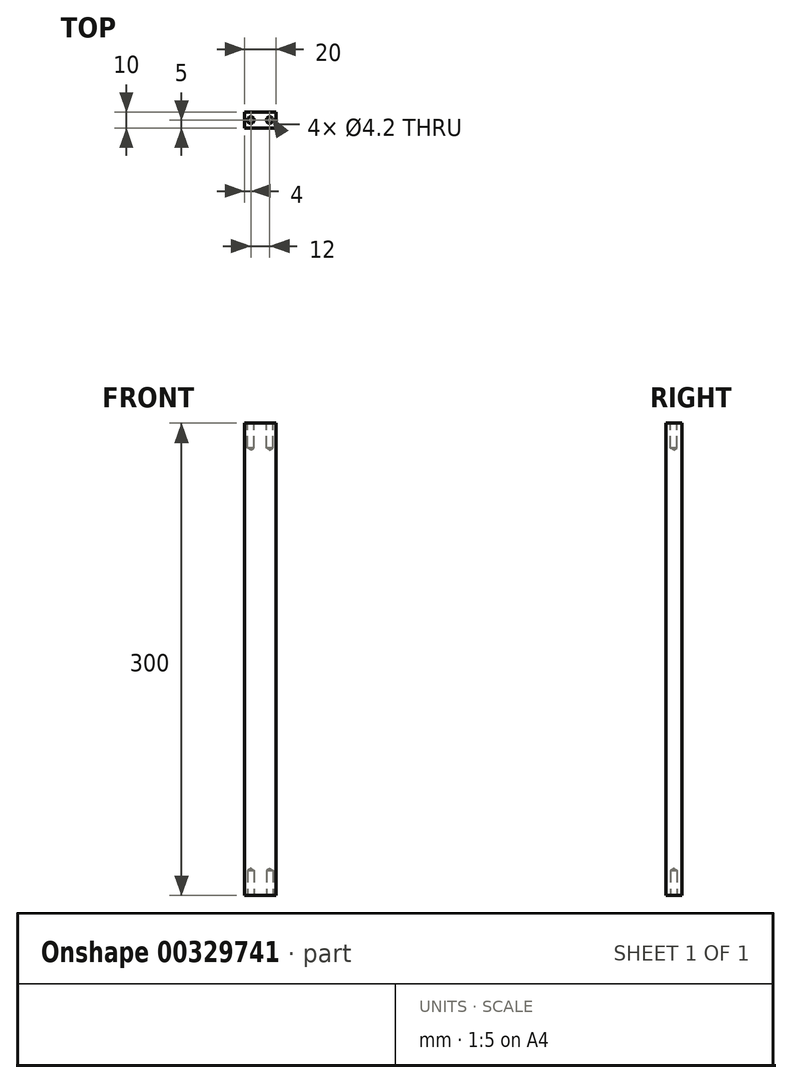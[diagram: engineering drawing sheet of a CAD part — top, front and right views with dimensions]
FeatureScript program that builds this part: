
annotation { "Feature Type Name" : "Feature", "Feature Type Description" : "" }
export const myFeature = defineFeature(function(context is Context, id is Id, definition is map)
    precondition{}
    {
        {
            var Q0;
            Q0=qCreatedBy(makeId("Front.planeOp"),FACE);
            var sketch = newSketch(context, id + "F0", { "sketchPlane" : qUnion([Q0])});
            skLineSegment(sketch, "E0.bottom", {"start": v(-10, 150) * mm, "end": v(10, 150) * mm});
            skLineSegment(sketch, "E0.top", {"start": v(-10, -150) * mm, "end": v(10, -150) * mm});
            skLineSegment(sketch, "E0.left", {"start": v(-10, 150) * mm, "end": v(-10, -150) * mm});
            skLineSegment(sketch, "E0.right", {"start": v(10, 150) * mm, "end": v(10, -150) * mm});
            skLineSegment(sketch, "E1", {"start": v(0, 25.89) * mm, "end": v(0, -35.08) * mm, "construction": true});
            skLineSegment(sketch, "E2", {"start": v(25.8, 0) * mm, "end": v(-25.16, 0) * mm, "construction": true});
            skSolve(sketch);
        }
        {
            var Q0;
            Q0=qSketchRegion(id+"F0",true);
            extrude(context, id + "F1", {"entities" : qUnion([Q0]), "depth" : 10 * mm});
        }
        {
            var Q0;
            Q0=makeQuery(id+"F1.opExtrude","SWEPT_FACE",FACE,{"disambiguationData":[OSD([sQuery(id+"F0.wireOp",EDGE,"E0.top")])]});
            var sketch = newSketch(context, id + "F2", { "sketchPlane" : qUnion([Q0])});
            skLineSegment(sketch, "E3", {"start": v(0, 35) * mm, "end": v(0, -22.14) * mm, "construction": true});
            skLineSegment(sketch, "E4", {"start": v(10, 5) * mm, "end": v(-16.26, 5) * mm, "construction": true});
            skPoint(sketch, "E5", {"position": v(-6, 5) * mm});
            skPoint(sketch, "E6.MirrorP", {"position": v(6, 5) * mm});
            skSolve(sketch);
        }
        {
            var Q0;
            Q0=sQuery(id+"F2.wireOp",VERTEX,"E5");
            var Q1;
            Q1=sQuery(id+"F2.wireOp",VERTEX,"E6.MirrorP");
            var Q2;
            Q2=makeQuery(id+"F1.opExtrude","SWEPT_BODY",BODY,{"disambiguationData":[OSD([sQuery(id+"F0.wireOp",EDGE,"E0.bottom"),sQuery(id+"F0.wireOp",EDGE,"E0.top"),sQuery(id+"F0.wireOp",EDGE,"E0.left"),sQuery(id+"F0.wireOp",EDGE,"E0.right")])]});
            hole(context, id + "F3", {"style" : HoleStyle.SIMPLE, "endStyle" : HoleEndStyle.BLIND, "standardTappedOrClearance" : lookupTablePath({ "standard" : "ISO", "engagement" : "75%", "pitch" : "0.8 mm", "size" : "M5", "type" : "Tapped" }), "standardBlindInLast" : lookupTablePath({ "standard" : "ISO", "engagement" : "75%", "pitch" : "0.8 mm", "size" : "M5", "type" : "Tapped" }), "holeDiameter" : 4.2 * mm, "showTappedDepth" : true, "holeDepth" : 15.8 * mm, "tappedDepth" : 15 * mm, "tapClearance" : 1, "locations" : qUnion([Q0, Q1]), "scope" : qUnion([Q2]), "majorDiameter" : 5 * mm});
        }
        {
            var Q0;
            Q0=makeQuery(id+"F1.opExtrude","SWEPT_FACE",FACE,{"disambiguationData":[OSD([sQuery(id+"F0.wireOp",EDGE,"E0.bottom")])]});
            var sketch = newSketch(context, id + "F4", { "sketchPlane" : qUnion([Q0])});
            skLineSegment(sketch, "E7", {"start": v(0, -19.56) * mm, "end": v(0, 13.4) * mm, "construction": true});
            skLineSegment(sketch, "E8", {"start": v(-10, -5) * mm, "end": v(11.43, -5) * mm, "construction": true});
            skPoint(sketch, "E8.endSnap0", {"position": v(10, -5) * mm});
            skPoint(sketch, "E9", {"position": v(6, -5) * mm});
            skPoint(sketch, "E10.MirrorP", {"position": v(-6, -5) * mm});
            skSolve(sketch);
        }
        {
            var Q0;
            Q0=sQuery(id+"F4.wireOp",VERTEX,"E9");
            var Q1;
            Q1=sQuery(id+"F4.wireOp",VERTEX,"E10.MirrorP");
            var Q2;
            Q2=makeQuery(id+"F1.opExtrude","SWEPT_BODY",BODY,{"disambiguationData":[OSD([sQuery(id+"F0.wireOp",EDGE,"E0.bottom"),sQuery(id+"F0.wireOp",EDGE,"E0.top"),sQuery(id+"F0.wireOp",EDGE,"E0.left"),sQuery(id+"F0.wireOp",EDGE,"E0.right")])]});
            hole(context, id + "F5", {"style" : HoleStyle.SIMPLE, "endStyle" : HoleEndStyle.BLIND, "standardTappedOrClearance" : lookupTablePath({ "standard" : "ISO", "engagement" : "75%", "pitch" : "0.8 mm", "size" : "M5", "type" : "Tapped" }), "standardBlindInLast" : lookupTablePath({ "standard" : "ISO", "engagement" : "75%", "pitch" : "0.8 mm", "size" : "M5", "type" : "Tapped" }), "holeDiameter" : 4.2 * mm, "showTappedDepth" : true, "holeDepth" : 15.8 * mm, "tappedDepth" : 15 * mm, "tapClearance" : 1, "locations" : qUnion([Q0, Q1]), "scope" : qUnion([Q2]), "majorDiameter" : 5 * mm});
        }
    });
